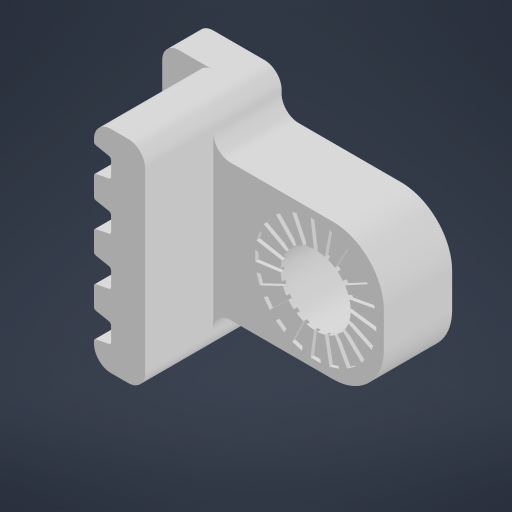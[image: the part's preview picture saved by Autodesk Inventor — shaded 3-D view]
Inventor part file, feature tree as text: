
AUTODESK INVENTOR PART (.ipt)
format: ipt  version: 2023 (Build 270158000, 158)  size: 480,256 bytes
history: native  units: mm
features: extrude x4, sketch x4, fillet x1, projected_geometry x1
ambient origin geometry x8: Origin, YZ Plane, XZ Plane, XY Plane, X Axis, Y Axis, Z Axis, Center Point
bodies: Body1 (feature_tree)
feature tree (10):
  extrude  "Extrusion2"  Depth=6.0mm TaperAngle=0.0deg
  extrude  "Extrusion3"  Depth=2.0mm
  extrude  "Extrusion4"  Depth=2.0mm
  fillet  "Fillet1"  Radius=2.0mm
  extrude  "Extrusion5"  Depth=4.0mm
  sketch  "Sketch2"  dims[d9=12.0mm d10=6.0mm d11=0.0mm]
  sketch  "Sketch4"  dims[d12=3.0mm d13=2.0mm]
  sketch  "Sketch5"  dims[d14=3.0mm d15=2.0mm d16=2.0mm d17=0.0mm]
  sketch  "Sketch8"  dims[d18=10.0mm d19=4.0mm d20=4.1mm d21=4.0mm d22=3.8mm d23=0.0mm d24=1.0mm d25=3.0mm d26=1.5mm d27=0.3mm d28=0.1mm d29=200.0mm d31=360.0deg d33=0.2mm d34=0.0mm d35=0.5mm d36=0.872665mm d37=0.5mm d38=0.872665mm]
  projected_geometry  "Projected Loop1"
